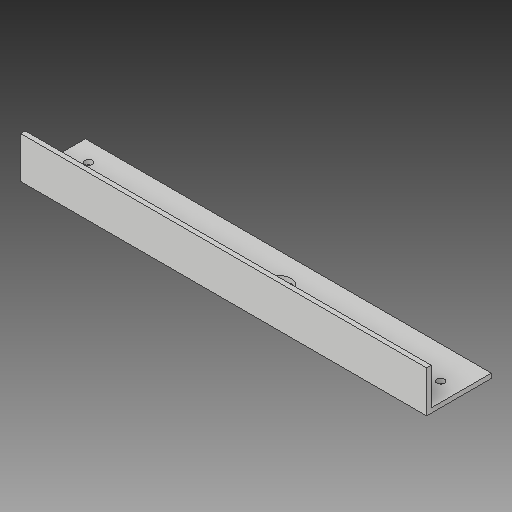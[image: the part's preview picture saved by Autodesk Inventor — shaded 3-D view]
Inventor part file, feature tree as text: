
AUTODESK INVENTOR PART (.ipt)
format: ipt  version: 2018 (Build 220112000, 112)  size: 105,472 bytes
history: native  units: in
note: dims shown in document units (in); Inventor stores cm internally (conversion verified against a paired STEP export)
features: sketch x4, other x3
ambient origin geometry x8: Origin, YZ Plane, XZ Plane, XY Plane, X Axis, Y Axis, Z Axis, Center Point
bodies: Solid1 (feature_tree)
feature tree (7):
  other  "angle iron with  holes 2_MIR.ipt"
  other  "Solid1::angle iron with  holes 2_MIR.ipt"
  other  "TaggingFeature1"
  sketch  "Sketch1"  dims[d0=0.3937in]
  sketch  "Sketch2"
  sketch  "Sketch3"
  sketch  "Sketch4"
